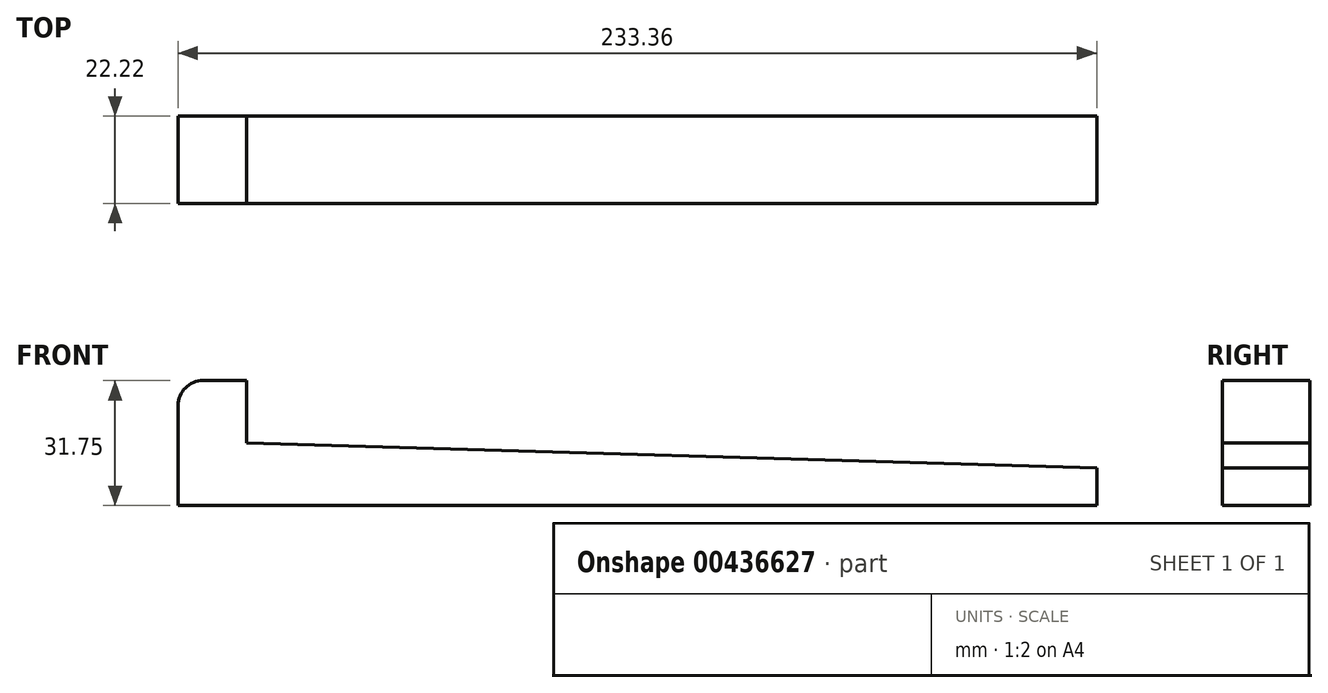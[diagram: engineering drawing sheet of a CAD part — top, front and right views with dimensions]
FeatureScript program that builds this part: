
annotation { "Feature Type Name" : "Feature", "Feature Type Description" : "" }
export const myFeature = defineFeature(function(context is Context, id is Id, definition is map)
    precondition{}
    {
        {
            var Q0;
            Q0=qCreatedBy(makeId("Front.planeOp"),FACE);
            var sketch = newSketch(context, id + "F0", { "sketchPlane" : qUnion([Q0])});
            skLineSegment(sketch, "E0", {"start": v(-89.74, 12.2) * mm, "end": v(143.62, 12.2) * mm});
            skLineSegment(sketch, "E1", {"start": v(-72.28, 28.08) * mm, "end": v(143.62, 21.73) * mm});
            skLineSegment(sketch, "E2", {"start": v(143.62, 21.73) * mm, "end": v(143.62, 12.2) * mm});
            skLineSegment(sketch, "E3", {"start": v(-72.28, 28.08) * mm, "end": v(-72.28, 43.96) * mm});
            skLineSegment(sketch, "E4", {"start": v(-89.74, 37.6) * mm, "end": v(-89.74, 12.2) * mm});
            skLineSegment(sketch, "E5", {"start": v(-83.4, 43.96) * mm, "end": v(-72.28, 43.96) * mm});
            skArc(sketch, "E6.filletArc", {"start": v(-83.4, 43.96) * mm, "mid": v(-87.88, 42.1) * mm, "end": v(-89.74, 37.6) * mm});
            skSolve(sketch);
        }
        {
            var Q0;
            Q0=makeQuery(id+"F0.imprint","IMPRINT",FACE,{"disambiguationData":[TD([[makeQuery(id+"F0.imprint","IMPRINT",EDGE,{"derivedFrom":sQuery(id+"F0.wireOp",EDGE,"E0")}),1.0]])]});
            extrude(context, id + "F1", {"entities" : qUnion([Q0]), "depth" : 22.22 * mm, "offsetDistance" : 25.4 * mm, "symmetric" : true});
        }
    });
